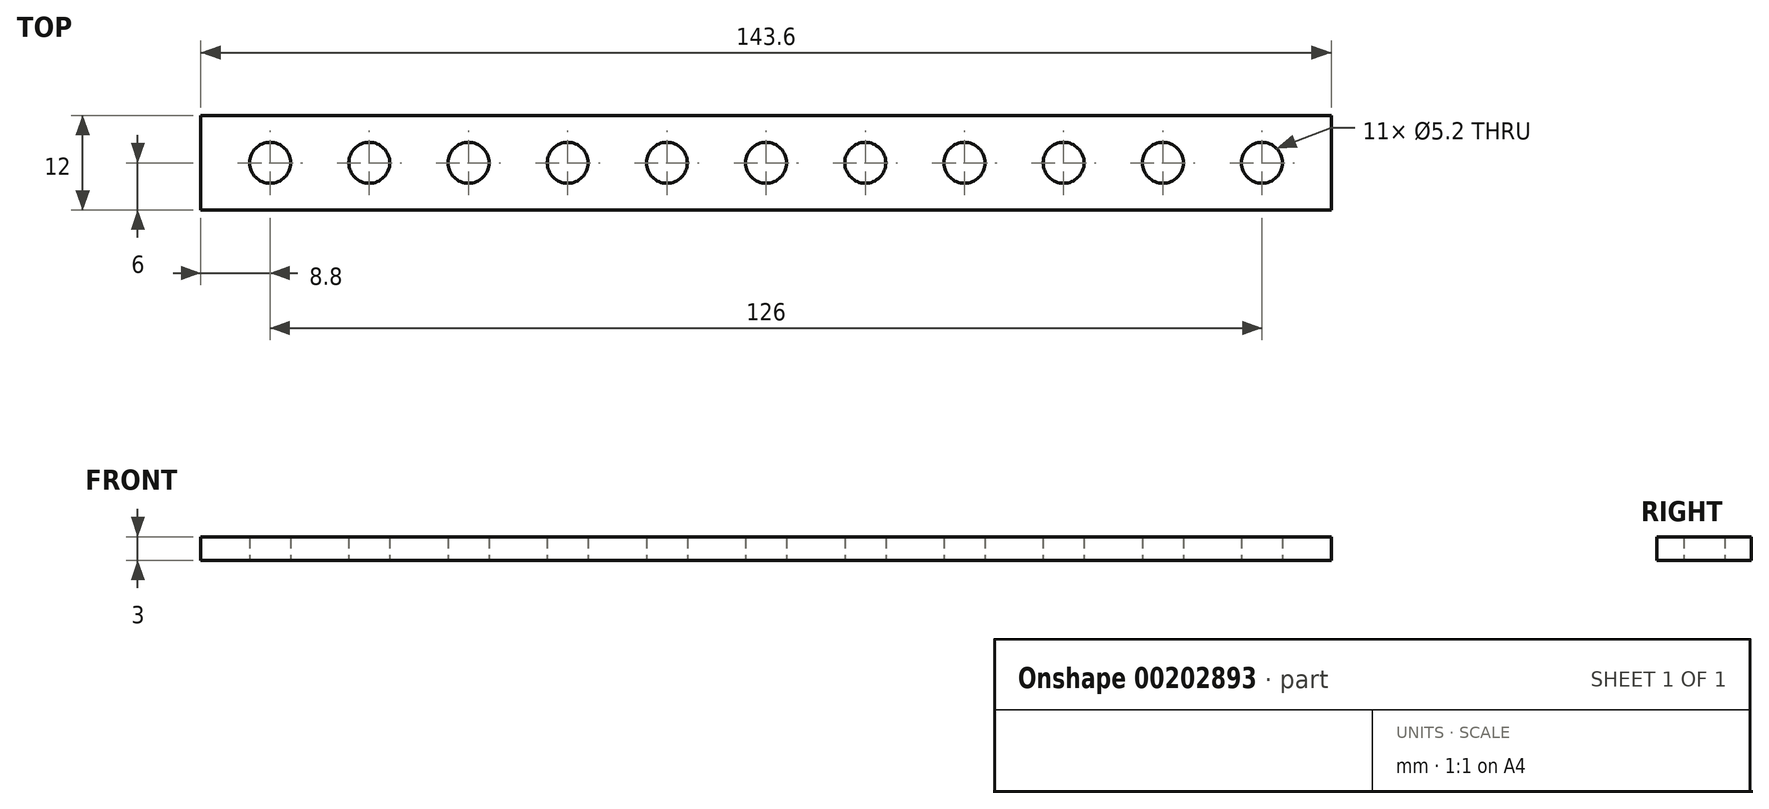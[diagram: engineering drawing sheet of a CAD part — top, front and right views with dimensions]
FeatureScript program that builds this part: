
annotation { "Feature Type Name" : "Feature", "Feature Type Description" : "" }
export const myFeature = defineFeature(function(context is Context, id is Id, definition is map)
    precondition{}
    {
        {
            var Q0;
            Q0=qCreatedBy(makeId("Top.planeOp"),FACE);
            var sketch = newSketch(context, id + "F0", { "sketchPlane" : qUnion([Q0])});
            skLineSegment(sketch, "E0", {"start": v(-71.8, 0) * mm, "end": v(57.8, 0) * mm, "construction": true});
            skLineSegment(sketch, "E1", {"start": v(-71.8, 0) * mm, "end": v(-71.8, 6) * mm});
            skLineSegment(sketch, "E2.MirrorCS", {"start": v(-71.8, 0) * mm, "end": v(-71.8, -6) * mm});
            skLineSegment(sketch, "E3", {"start": v(-63, 17.87) * mm, "end": v(-63, -27.5) * mm, "construction": true});
            skLineSegment(sketch, "E4", {"start": v(-50.31, 19.64) * mm, "end": v(-50.31, -29.06) * mm, "construction": true});
            skCircle(sketch, "E5", {"center": v(-63, 0) * mm, "radius": 2.6 * mm});
            skLineSegment(sketch, "E6.1.0.0", {"start": v(-50.4, 17.87) * mm, "end": v(-50.4, -27.5) * mm, "construction": true});
            skCircle(sketch, "E6.1.0.1", {"center": v(-50.4, 0) * mm, "radius": 2.6 * mm});
            skLineSegment(sketch, "E6.2.0.0", {"start": v(-37.8, 17.87) * mm, "end": v(-37.8, -27.5) * mm, "construction": true});
            skCircle(sketch, "E6.2.0.1", {"center": v(-37.8, 0) * mm, "radius": 2.6 * mm});
            skLineSegment(sketch, "E6.3.0.0", {"start": v(-25.2, 17.87) * mm, "end": v(-25.2, -27.5) * mm, "construction": true});
            skCircle(sketch, "E6.3.0.1", {"center": v(-25.2, 0) * mm, "radius": 2.6 * mm});
            skLineSegment(sketch, "E6.4.0.0", {"start": v(-12.6, 17.87) * mm, "end": v(-12.6, -27.5) * mm, "construction": true});
            skCircle(sketch, "E6.4.0.1", {"center": v(-12.6, 0) * mm, "radius": 2.6 * mm});
            skLineSegment(sketch, "E6.5.0.0", {"start": v(0, 17.87) * mm, "end": v(0, -27.5) * mm, "construction": true});
            skCircle(sketch, "E6.5.0.1", {"center": v(0, 0) * mm, "radius": 2.6 * mm});
            skLineSegment(sketch, "E6.6.0.0", {"start": v(12.6, 17.87) * mm, "end": v(12.6, -27.5) * mm, "construction": true});
            skCircle(sketch, "E6.6.0.1", {"center": v(12.6, 0) * mm, "radius": 2.6 * mm});
            skLineSegment(sketch, "E6.7.0.0", {"start": v(25.2, 17.87) * mm, "end": v(25.2, -27.5) * mm, "construction": true});
            skCircle(sketch, "E6.7.0.1", {"center": v(25.2, 0) * mm, "radius": 2.6 * mm});
            skLineSegment(sketch, "E6.8.0.0", {"start": v(37.8, 17.87) * mm, "end": v(37.8, -27.5) * mm, "construction": true});
            skCircle(sketch, "E6.8.0.1", {"center": v(37.8, 0) * mm, "radius": 2.6 * mm});
            skLineSegment(sketch, "E6.9.0.0", {"start": v(50.4, 17.87) * mm, "end": v(50.4, -27.5) * mm, "construction": true});
            skCircle(sketch, "E6.9.0.1", {"center": v(50.4, 0) * mm, "radius": 2.6 * mm});
            skLineSegment(sketch, "E6.10.0.0", {"start": v(63, 17.87) * mm, "end": v(63, -27.5) * mm, "construction": true});
            skCircle(sketch, "E6.10.0.1", {"center": v(63, 0) * mm, "radius": 2.6 * mm});
            skLineSegment(sketch, "E6.direction1", {"start": v(-63, -27.5) * mm, "end": v(-50.4, -27.5) * mm, "construction": true});
            skLineSegment(sketch, "E7", {"start": v(0, 44.26) * mm, "end": v(0, -41.64) * mm, "construction": true});
            skLineSegment(sketch, "E8.MirrorCS", {"start": v(71.8, 0) * mm, "end": v(71.8, 6) * mm});
            skLineSegment(sketch, "E9.MirrorCS", {"start": v(71.8, 0) * mm, "end": v(71.8, -6) * mm});
            skLineSegment(sketch, "E10", {"start": v(-71.8, 6) * mm, "end": v(71.8, 6) * mm});
            skLineSegment(sketch, "E11", {"start": v(-71.8, -6) * mm, "end": v(71.8, -6) * mm});
            skSolve(sketch);
        }
        {
            var Q0;
            Q0 = qSketchRegion(id + "F0", true);
            extrude(context, id + "F1", {"entities" : qUnion([Q0]), "depth" : 3 * mm});
        }
    });
